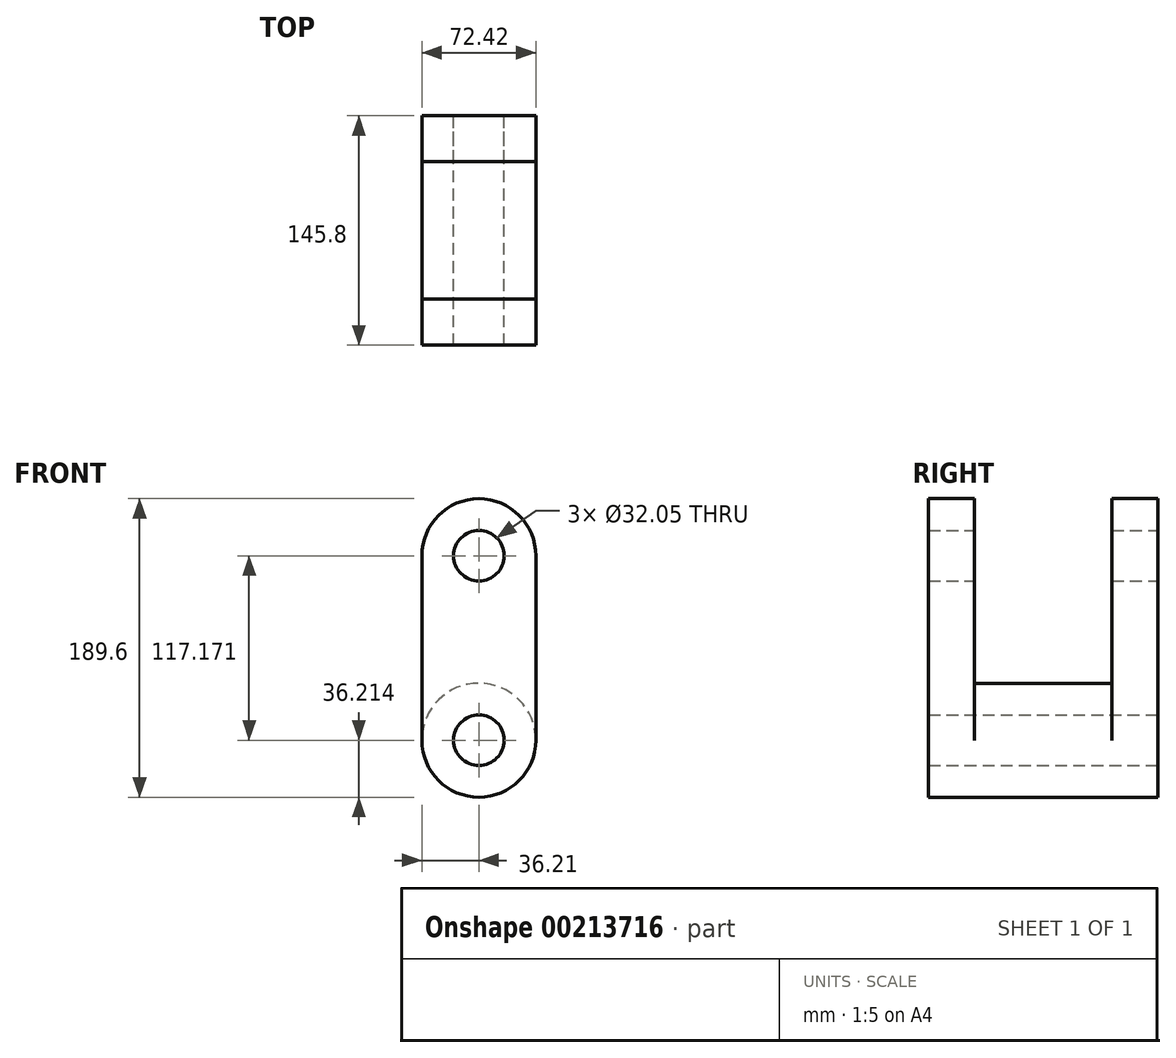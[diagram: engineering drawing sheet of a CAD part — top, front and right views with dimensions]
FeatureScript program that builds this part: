
annotation { "Feature Type Name" : "Feature", "Feature Type Description" : "" }
export const myFeature = defineFeature(function(context is Context, id is Id, definition is map)
    precondition{}
    {
        {
            var Q0;
            Q0=qCreatedBy(makeId("Front.planeOp"),FACE);
            var sketch = newSketch(context, id + "F0", { "sketchPlane" : qUnion([Q0])});
            skLineSegment(sketch, "E0.bottom", {"start": v(36.21, -58.59) * mm, "end": v(-36.21, -58.59) * mm});
            skLineSegment(sketch, "E0.top", {"start": v(36.21, 58.59) * mm, "end": v(-36.21, 58.59) * mm});
            skLineSegment(sketch, "E0.left", {"start": v(36.21, -58.59) * mm, "end": v(36.21, 58.59) * mm});
            skLineSegment(sketch, "E0.right", {"start": v(-36.21, -58.59) * mm, "end": v(-36.21, 58.59) * mm});
            skPoint(sketch, "E0.middle", {"position": v(0, 0) * mm});
            skCircle(sketch, "E1", {"center": v(0, 58.59) * mm, "radius": 36.21 * mm});
            skCircle(sketch, "E2", {"center": v(0, -58.59) * mm, "radius": 36.21 * mm});
            skCircle(sketch, "E3", {"center": v(0, 58.59) * mm, "radius": 16.02 * mm});
            skCircle(sketch, "E4", {"center": v(0, -58.59) * mm, "radius": 16.02 * mm});
            skSolve(sketch);
        }
        {
            var Q0;
            {var subQ1=sQuery(id+"F0.wireOp",EDGE,"E0.top");var subQ3=sQuery(id+"F0.wireOp",EDGE,"E3");var subQ4=makeQuery(id+"F0.imprint","INTERSECT",VERTEX,{"disambiguationData":[OD(0.0)],"derivedFrom":[subQ1,subQ3]});Q0=makeQuery(id+"F0.imprint","IMPRINT",FACE,{"disambiguationData":[TD([[makeQuery(id+"F0.imprint","IMPRINT",EDGE,{"disambiguationData":[TD([[subQ4,-1.0]])],"derivedFrom":subQ3}),-1.0]])]});}
            var Q1;
            {var subQ1=sQuery(id+"F0.wireOp",EDGE,"E0.top");var subQ3=sQuery(id+"F0.wireOp",EDGE,"E3");var subQ4=makeQuery(id+"F0.imprint","INTERSECT",VERTEX,{"disambiguationData":[OD(0.0)],"derivedFrom":[subQ1,subQ3]});Q1=makeQuery(id+"F0.imprint","IMPRINT",FACE,{"disambiguationData":[TD([[makeQuery(id+"F0.imprint","IMPRINT",EDGE,{"disambiguationData":[TD([[subQ4,1.0]])],"derivedFrom":subQ3}),-1.0]])]});}
            var Q2;
            {var subQ0=sQuery(id+"F0.wireOp",EDGE,"E0.left");Q2=makeQuery(id+"F0.imprint","IMPRINT",FACE,{"disambiguationData":[TD([[makeQuery(id+"F0.imprint","IMPRINT",EDGE,{"derivedFrom":subQ0}),1.0]])]});}
            var Q3;
            {var subQ1=sQuery(id+"F0.wireOp",EDGE,"E0.bottom");var subQ3=sQuery(id+"F0.wireOp",EDGE,"E4");var subQ4=makeQuery(id+"F0.imprint","INTERSECT",VERTEX,{"disambiguationData":[OD(0.0)],"derivedFrom":[subQ1,subQ3]});Q3=makeQuery(id+"F0.imprint","IMPRINT",FACE,{"disambiguationData":[TD([[makeQuery(id+"F0.imprint","IMPRINT",EDGE,{"disambiguationData":[TD([[subQ4,-1.0]])],"derivedFrom":subQ3}),-1.0]])]});}
            var Q4;
            {var subQ1=sQuery(id+"F0.wireOp",EDGE,"E0.bottom");var subQ3=sQuery(id+"F0.wireOp",EDGE,"E4");var subQ4=makeQuery(id+"F0.imprint","INTERSECT",VERTEX,{"disambiguationData":[OD(0.0)],"derivedFrom":[subQ1,subQ3]});Q4=makeQuery(id+"F0.imprint","IMPRINT",FACE,{"disambiguationData":[TD([[makeQuery(id+"F0.imprint","IMPRINT",EDGE,{"disambiguationData":[TD([[subQ4,1.0]])],"derivedFrom":subQ3}),-1.0]])]});}
            extrude(context, id + "F1", {"entities" : qUnion([Q0, Q1, Q2, Q3, Q4]), "depth" : 145.8 * mm, "symmetric" : true});
        }
        {
            var Q0;
            {var subQ1=sQuery(id+"F0.wireOp",EDGE,"E0.top");var subQ3=sQuery(id+"F0.wireOp",EDGE,"E3");var subQ4=makeQuery(id+"F0.imprint","INTERSECT",VERTEX,{"disambiguationData":[OD(0.0)],"derivedFrom":[subQ1,subQ3]});Q0=makeQuery(id+"F0.imprint","IMPRINT",FACE,{"disambiguationData":[TD([[makeQuery(id+"F0.imprint","IMPRINT",EDGE,{"disambiguationData":[TD([[subQ4,-1.0]])],"derivedFrom":subQ3}),-1.0]])]});}
            var Q1;
            {var subQ1=sQuery(id+"F0.wireOp",EDGE,"E0.top");var subQ3=sQuery(id+"F0.wireOp",EDGE,"E3");var subQ4=makeQuery(id+"F0.imprint","INTERSECT",VERTEX,{"disambiguationData":[OD(0.0)],"derivedFrom":[subQ1,subQ3]});Q1=makeQuery(id+"F0.imprint","IMPRINT",FACE,{"disambiguationData":[TD([[makeQuery(id+"F0.imprint","IMPRINT",EDGE,{"disambiguationData":[TD([[subQ4,1.0]])],"derivedFrom":subQ3}),-1.0]])]});}
            var Q2;
            {var subQ0=sQuery(id+"F0.wireOp",EDGE,"E0.left");Q2=makeQuery(id+"F0.imprint","IMPRINT",FACE,{"disambiguationData":[TD([[makeQuery(id+"F0.imprint","IMPRINT",EDGE,{"derivedFrom":subQ0}),1.0]])]});}
            extrude(context, id + "F2", {"entities" : qUnion([Q0, Q1, Q2]), "operationType" : NewBodyOperationType.REMOVE, "oppositeDirection" : true, "depth" : 87.38 * mm, "symmetric" : true});
        }
    });
